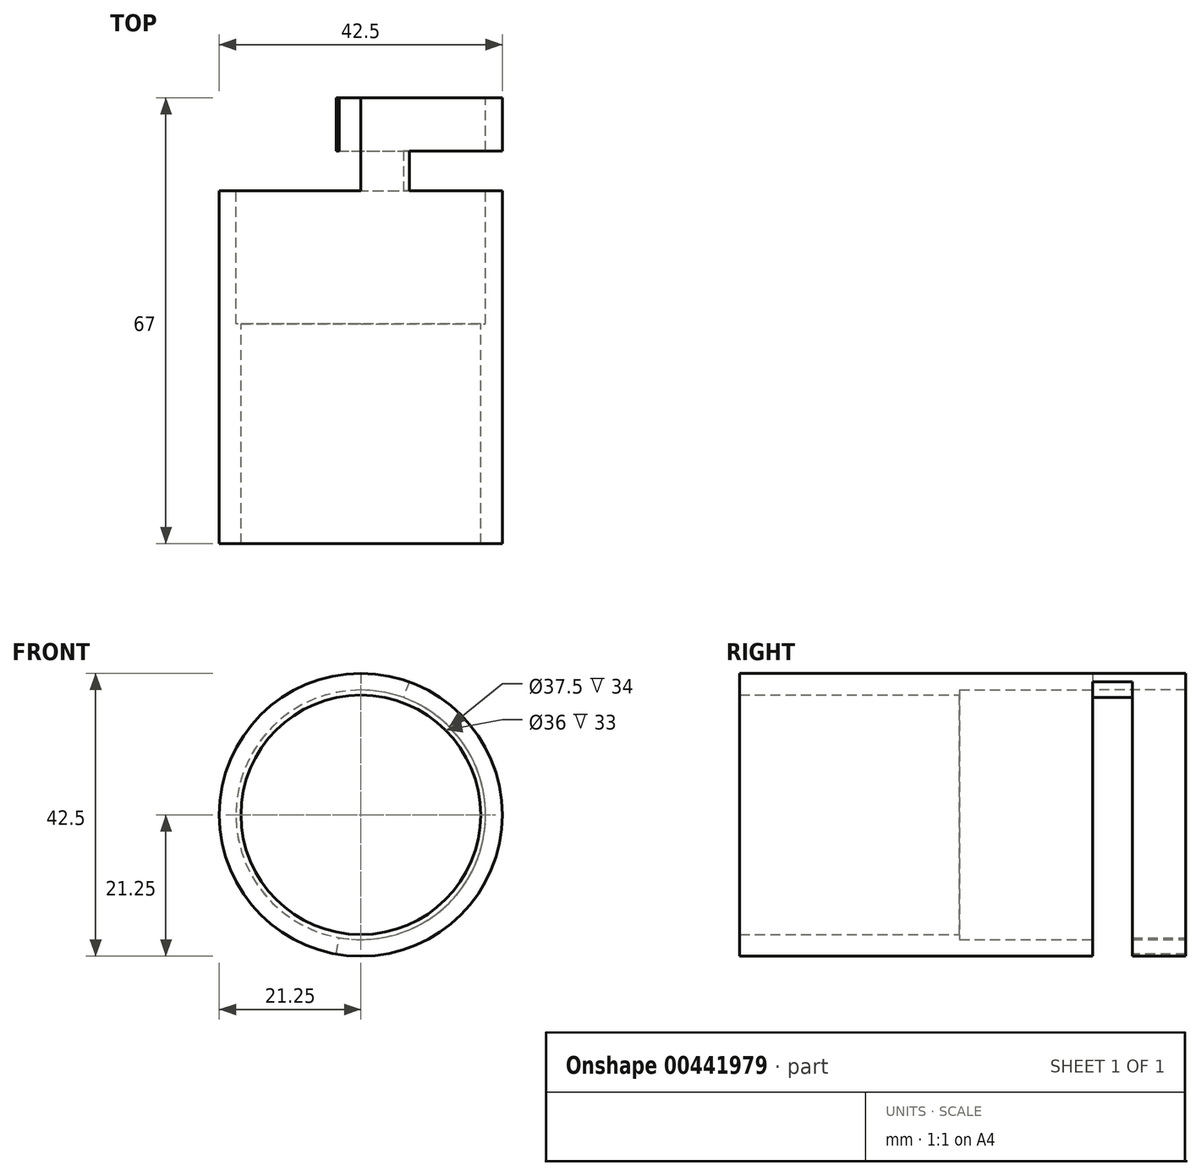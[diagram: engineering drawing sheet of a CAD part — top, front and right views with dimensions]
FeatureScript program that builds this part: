
annotation { "Feature Type Name" : "Feature", "Feature Type Description" : "" }
export const myFeature = defineFeature(function(context is Context, id is Id, definition is map)
    precondition{}
    {
        {
            var Q0;
            Q0=qCreatedBy(makeId("Front.planeOp"),FACE);
            var sketch = newSketch(context, id + "F0", { "sketchPlane" : qUnion([Q0])});
            skCircle(sketch, "E0", {"center": v(0, 0) * mm, "radius": 18.75 * mm});
            skCircle(sketch, "E1", {"center": v(0, 0) * mm, "radius": 21.25 * mm});
            skSolve(sketch);
        }
        {
            var Q0;
            Q0 = qSketchRegion(id + "F0", true);
            extrude(context, id + "F1", {"entities" : qUnion([Q0]), "depth" : 20 * mm});
        }
        {
            var Q0;
            Q0=qCreatedBy(makeId("Front.planeOp"),FACE);
            cPlane(context, id + "F2", {"entities" : qUnion([Q0]), "cplaneType" : CPlaneType.OFFSET, "offset" : 28 * mm, "width" : 150 * mm, "height" : 150 * mm});
        }
        {
            var Q0;
            Q0=qCreatedBy(id+"F2.planeOp",FACE);
            var sketch = newSketch(context, id + "F3", { "sketchPlane" : qUnion([Q0])});
            skCircle(sketch, "E2", {"center": v(0, 0) * mm, "radius": 18 * mm});
            skCircle(sketch, "E3", {"center": v(0, 0) * mm, "radius": 21.25 * mm});
            skSolve(sketch);
        }
        {
            var Q0;
            Q0 = qSketchRegion(id + "F3", true);
            extrude(context, id + "F4", {"entities" : qUnion([Q0]), "depth" : 25 * mm});
        }
        {
            var Q0;
            Q0=makeQuery(id+"F4.opExtrude","CAP_FACE",FACE,{"disambiguationData":[OSD([sQuery(id+"F3.wireOp",EDGE,"E2"),sQuery(id+"F3.wireOp",EDGE,"E3")])],"isStart":true});
            var Q1;
            Q1=makeQuery(id+"F1.opExtrude","CAP_FACE",FACE,{"disambiguationData":[OSD([sQuery(id+"F0.wireOp",EDGE,"E0"),sQuery(id+"F0.wireOp",EDGE,"E1")])],"isStart":false});
            extrude(context, id + "F5", {"entities" : qUnion([Q0]), "endBound" : BoundingType.UP_TO_SURFACE, "endBoundEntityFace" : qUnion([Q1]), "depth" : 25 * mm});
        }
        {
            var Q0;
            Q0=makeQuery(id+"F1.opExtrude","SWEPT_BODY",BODY,{"disambiguationData":[OSD([sQuery(id+"F0.wireOp",EDGE,"E0"),sQuery(id+"F0.wireOp",EDGE,"E1")])]});
            var Q1;
            Q1=makeQuery(id+"F4.opExtrude","SWEPT_BODY",BODY,{"disambiguationData":[OSD([sQuery(id+"F3.wireOp",EDGE,"E2"),sQuery(id+"F3.wireOp",EDGE,"E3")])]});
            var Q2;
            Q2=makeQuery(id+"F5.opExtrude","SWEPT_BODY",BODY,{"disambiguationData":[OSD([sQuery(id+"F3.wireOp",EDGE,"E2"),sQuery(id+"F3.wireOp",EDGE,"E3")])]});
            booleanBodies(context, id + "F6", {"operationType" : BooleanOperationType.UNION, "tools" : qUnion([Q0, Q1, Q2])});
        }
        {
            var Q0;
            Q0=qCreatedBy(makeId("Right.planeOp"),FACE);
            var sketch = newSketch(context, id + "F7", { "sketchPlane" : qUnion([Q0])});
            skLineSegment(sketch, "E4", {"start": v(0, 21.25) * mm, "end": v(6, 21.25) * mm});
            skLineSegment(sketch, "E5", {"start": v(6, 21.25) * mm, "end": v(6, 18.75) * mm});
            skLineSegment(sketch, "E6", {"start": v(6, 18.75) * mm, "end": v(0, 18.75) * mm});
            skLineSegment(sketch, "E7", {"start": v(0, 21.25) * mm, "end": v(0, 18.75) * mm});
            skLineSegment(sketch, "E8", {"start": v(0.53, 0) * mm, "end": v(12.72, 0) * mm});
            skSolve(sketch);
        }
        {
            var Q0;
            Q0 = qSketchRegion(id + "F7", true);
            var Q1;
            Q1=sQuery(id+"F7.wireOp",EDGE,"E8");
            revolve(context, id + "F8", {"operationType" : NewBodyOperationType.ADD, "entities" : qUnion([Q0]), "axis" : qUnion([Q1]), "revolveType" : RevolveType.ONE_DIRECTION, "angle" : 20 * degree});
        }
        {
            var Q0;
            Q0=makeQuery(id+"F8.opRevolve","CAP_FACE",FACE,{"disambiguationData":[OSD([sQuery(id+"F7.wireOp",EDGE,"E4"),sQuery(id+"F7.wireOp",EDGE,"E5"),sQuery(id+"F7.wireOp",EDGE,"E6"),sQuery(id+"F7.wireOp",EDGE,"E7")])],"isStart":true});
            var sketch = newSketch(context, id + "F9", { "sketchPlane" : qUnion([Q0])});
            skLineSegment(sketch, "E9", {"start": v(-14, 21.25) * mm, "end": v(-6, 21.25) * mm});
            skLineSegment(sketch, "E10", {"start": v(-6, 21.25) * mm, "end": v(-6, 18.75) * mm});
            skLineSegment(sketch, "E11", {"start": v(-6, 18.75) * mm, "end": v(-14, 18.75) * mm});
            skLineSegment(sketch, "E12", {"start": v(-14, 18.75) * mm, "end": v(-14, 21.25) * mm});
            skLineSegment(sketch, "E13", {"start": v(0, 0) * mm, "end": v(-17.82, 0) * mm});
            skSolve(sketch);
        }
        {
            var Q0;
            Q0 = qSketchRegion(id + "F9", true);
            var Q1;
            Q1=sQuery(id+"F9.wireOp",EDGE,"E13");
            revolve(context, id + "F10", {"operationType" : NewBodyOperationType.ADD, "entities" : qUnion([Q0]), "axis" : qUnion([Q1]), "revolveType" : RevolveType.ONE_DIRECTION, "angle" : 190 * degree});
        }
    });
